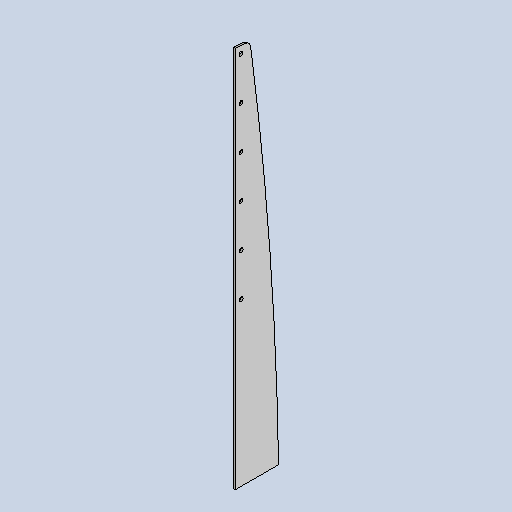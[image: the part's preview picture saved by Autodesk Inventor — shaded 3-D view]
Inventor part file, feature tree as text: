
AUTODESK INVENTOR PART (.ipt)
format: ipt  version: 2025 (Build 290162010, 162A)  size: 140,800 bytes
history: native  units: mm
features: sketch x2, other x2, sheet_metal_op x1, chamfer x1, extrude x1, pattern_linear x1
ambient origin geometry x8: Origin, YZ Plane, XZ Plane, XY Plane, X Axis, Y Axis, Z Axis, Center Point
bodies: Solid1 (feature_tree)
feature tree (8):
  sheet_metal_op  "Face1"
  chamfer  "Corner Round3"
  extrude  "Extrusion1"  Depth=5650.0mm
  pattern_linear  "Rectangular Pattern2"  Spacing1=14.870205mm  [1 undecoded]
  sketch  "Sketch1"  dims[d2=25.0mm d3=5650.0mm]
  other  "Plate1"
  sketch  "Sketch4"  dims[d4=3.0mm d7=14.870205mm d8=14.870205mm d9=10.0mm d23=7.0mm d25=10.0mm d26=0.0mm d27=0.0mm d29=60.0mm d31=72.5mm d32=13.0mm d33=97.0mm d34=651.812mm]
  other  "Definition1"
note: 1 required parameter value undecoded (feature->parameter linkage not recoverable at this tier; creation-order binding heuristic only, values carry confidence <= 0.55)
